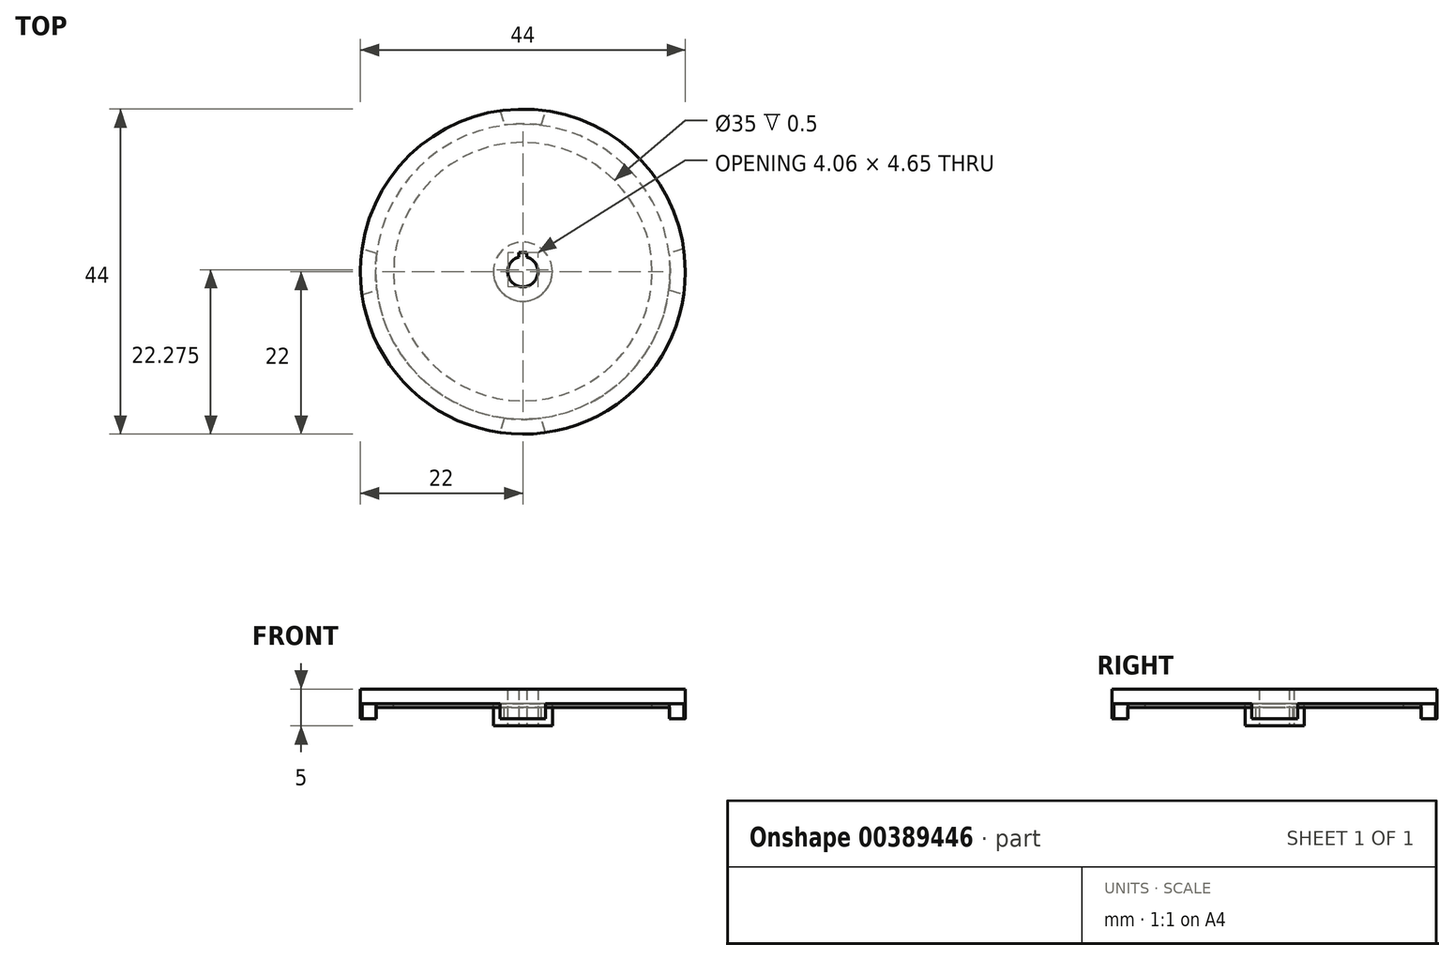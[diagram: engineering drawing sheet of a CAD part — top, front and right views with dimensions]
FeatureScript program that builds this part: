
annotation { "Feature Type Name" : "Feature", "Feature Type Description" : "" }
export const myFeature = defineFeature(function(context is Context, id is Id, definition is map)
    precondition{}
    {
        {
            var Q0;
            Q0=qCreatedBy(makeId("Top.planeOp"),FACE);
            var sketch = newSketch(context, id + "F0", { "sketchPlane" : qUnion([Q0])});
            skCircle(sketch, "E0", {"center": v(0, 0) * mm, "radius": 22 * mm});
            skArc(sketch, "E1", {"start": v(-0.55, 1.97) * mm, "mid": v(0, -2.05) * mm, "end": v(0.55, 1.97) * mm});
            skLineSegment(sketch, "E2.bottom", {"start": v(0.55, 2.6) * mm, "end": v(-0.55, 2.6) * mm});
            skLineSegment(sketch, "E2.left", {"start": v(0.55, 2.6) * mm, "end": v(0.55, 1.97) * mm});
            skLineSegment(sketch, "E2.right", {"start": v(-0.55, 2.6) * mm, "end": v(-0.55, 1.97) * mm});
            skSolve(sketch);
        }
        {
            var Q0;
            Q0=qSketchRegion(id+"F0",true);
            extrude(context, id + "F1", {"entities" : qUnion([Q0]), "depth" : 2 * mm});
        }
        {
            var Q0;
            Q0=makeQuery(id+"F1.opExtrude","CAP_FACE",FACE,{"disambiguationData":[OSD([sQuery(id+"F0.wireOp",EDGE,"E0")])],"isStart":true});
            var sketch = newSketch(context, id + "F2", { "sketchPlane" : qUnion([Q0])});
            skArc(sketch, "E3", {"start": v(-2.5, 19.84) * mm, "mid": v(-1.25, 19.96) * mm, "end": v(0, 20) * mm});
            skArc(sketch, "E4", {"start": v(0, 20) * mm, "mid": v(1.25, 19.96) * mm, "end": v(2.5, 19.84) * mm});
            skLineSegment(sketch, "E5", {"start": v(-2.5, 19.84) * mm, "end": v(-2.8, 20.81) * mm});
            skLineSegment(sketch, "E6", {"start": v(2.8, 20.81) * mm, "end": v(2.5, 19.84) * mm});
            skLineSegment(sketch, "E7", {"start": v(-2.8, 20.81) * mm, "end": v(-3.1, 21.78) * mm});
            skLineSegment(sketch, "E8", {"start": v(2.8, 20.81) * mm, "end": v(3.1, 21.78) * mm});
            skArc(sketch, "E9", {"start": v(-3.1, 21.78) * mm, "mid": v(0, 22) * mm, "end": v(3.1, 21.78) * mm});
            skLineSegment(sketch, "E10.1.0", {"start": v(-20.81, 2.8) * mm, "end": v(-21.78, 3.1) * mm});
            skArc(sketch, "E10.1.1", {"start": v(-20, 0) * mm, "mid": v(-19.96, 1.25) * mm, "end": v(-19.84, 2.5) * mm});
            skArc(sketch, "E10.1.2", {"start": v(-19.84, -2.5) * mm, "mid": v(-19.96, -1.25) * mm, "end": v(-20, 0) * mm});
            skLineSegment(sketch, "E10.1.3", {"start": v(-19.84, -2.5) * mm, "end": v(-20.81, -2.8) * mm});
            skLineSegment(sketch, "E10.1.4", {"start": v(-20.81, -2.8) * mm, "end": v(-21.78, -3.1) * mm});
            skArc(sketch, "E10.1.5", {"start": v(-21.78, -3.1) * mm, "mid": v(-22, 0) * mm, "end": v(-21.78, 3.1) * mm});
            skLineSegment(sketch, "E10.1.6", {"start": v(-20.81, 2.8) * mm, "end": v(-19.84, 2.5) * mm});
            skLineSegment(sketch, "E10.2.0", {"start": v(-2.8, -20.81) * mm, "end": v(-3.1, -21.78) * mm});
            skArc(sketch, "E10.2.1", {"start": v(0, -20) * mm, "mid": v(-1.25, -19.96) * mm, "end": v(-2.5, -19.84) * mm});
            skArc(sketch, "E10.2.2", {"start": v(2.5, -19.84) * mm, "mid": v(1.25, -19.96) * mm, "end": v(0, -20) * mm});
            skLineSegment(sketch, "E10.2.3", {"start": v(2.5, -19.84) * mm, "end": v(2.8, -20.81) * mm});
            skLineSegment(sketch, "E10.2.4", {"start": v(2.8, -20.81) * mm, "end": v(3.1, -21.78) * mm});
            skArc(sketch, "E10.2.5", {"start": v(3.1, -21.78) * mm, "mid": v(0, -22) * mm, "end": v(-3.1, -21.78) * mm});
            skLineSegment(sketch, "E10.2.6", {"start": v(-2.8, -20.81) * mm, "end": v(-2.5, -19.84) * mm});
            skLineSegment(sketch, "E10.3.0", {"start": v(20.81, -2.8) * mm, "end": v(21.78, -3.1) * mm});
            skArc(sketch, "E10.3.1", {"start": v(20, 0) * mm, "mid": v(19.96, -1.25) * mm, "end": v(19.84, -2.5) * mm});
            skArc(sketch, "E10.3.2", {"start": v(19.84, 2.5) * mm, "mid": v(19.96, 1.25) * mm, "end": v(20, 0) * mm});
            skLineSegment(sketch, "E10.3.3", {"start": v(19.84, 2.5) * mm, "end": v(20.81, 2.8) * mm});
            skLineSegment(sketch, "E10.3.4", {"start": v(20.81, 2.8) * mm, "end": v(21.78, 3.1) * mm});
            skArc(sketch, "E10.3.5", {"start": v(21.78, 3.1) * mm, "mid": v(22, 0) * mm, "end": v(21.78, -3.1) * mm});
            skLineSegment(sketch, "E10.3.6", {"start": v(20.81, -2.8) * mm, "end": v(19.84, -2.5) * mm});
            skSolve(sketch);
        }
        {
            var Q0;
            Q0=qSketchRegion(id+"F2",true);
            extrude(context, id + "F3", {"entities" : qUnion([Q0]), "operationType" : NewBodyOperationType.ADD, "depth" : 2 * mm});
        }
        {
            var Q0;
            Q0=makeQuery(id+"F1.opExtrude","CAP_FACE",FACE,{"disambiguationData":[OSD([sQuery(id+"F0.wireOp",EDGE,"E0"),sQuery(id+"F0.wireOp",EDGE,"E1"),sQuery(id+"F0.wireOp",EDGE,"E2.bottom"),sQuery(id+"F0.wireOp",EDGE,"E2.left"),sQuery(id+"F0.wireOp",EDGE,"E2.right")])],"isStart":true});
            var sketch = newSketch(context, id + "F4", { "sketchPlane" : qUnion([Q0])});
            skCircle(sketch, "E11", {"center": v(0, 0) * mm, "radius": 19.95 * mm});
            skCircle(sketch, "E12", {"center": v(0, 0) * mm, "radius": 17.5 * mm});
            skSolve(sketch);
        }
        {
            var Q0;
            Q0=qSketchRegion(id+"F4",true);
            extrude(context, id + "F5", {"entities" : qUnion([Q0]), "operationType" : NewBodyOperationType.ADD, "depth" : 0.5 * mm});
        }
        {
            var Q0;
            {var subQ0=sQuery(id+"F0.wireOp",EDGE,"E2.right");var subQ1=sQuery(id+"F0.wireOp",EDGE,"E2.left");var subQ2=sQuery(id+"F0.wireOp",EDGE,"E2.bottom");var subQ3=sQuery(id+"F0.wireOp",EDGE,"E1");Q0=makeQuery(id+"F5.boolean.opBoolean","SPLIT",FACE,{"disambiguationData":[TD([makeQuery(id+"F1.opExtrude","SWEPT_FACE",FACE,{"disambiguationData":[OSD([subQ3])]})])],"derivedFrom":makeQuery(id+"F1.opExtrude","CAP_FACE",FACE,{"disambiguationData":[OSD([sQuery(id+"F0.wireOp",EDGE,"E0"),subQ3,subQ2,subQ1,subQ0])],"isStart":true})});}
            var sketch = newSketch(context, id + "F6", { "sketchPlane" : qUnion([Q0])});
            skArc(sketch, "E13", {"start": v(0.55, -1.97) * mm, "mid": v(0, 2.05) * mm, "end": v(-0.55, -1.97) * mm});
            skCircle(sketch, "E14", {"center": v(0, 0) * mm, "radius": 4 * mm});
            skLineSegment(sketch, "E15", {"start": v(-0.55, -1.97) * mm, "end": v(-0.55, -2.6) * mm});
            skLineSegment(sketch, "E16", {"start": v(-0.55, -2.6) * mm, "end": v(0.55, -2.6) * mm});
            skLineSegment(sketch, "E17", {"start": v(0.55, -2.6) * mm, "end": v(0.55, -1.97) * mm});
            skSolve(sketch);
        }
        {
            var Q0;
            Q0=qSketchRegion(id+"F6",true);
            extrude(context, id + "F7", {"entities" : qUnion([Q0]), "operationType" : NewBodyOperationType.ADD, "depth" : 3 * mm});
        }
    });
